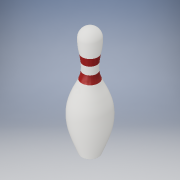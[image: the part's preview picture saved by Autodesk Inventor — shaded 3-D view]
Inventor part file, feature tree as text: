
AUTODESK INVENTOR PART (.ipt)
format: ipt  version: 2017 (Build 210142000, 142)  size: 568,832 bytes
history: native  units: in
note: dims shown in document units (in); Inventor stores cm internally (conversion verified against a paired STEP export)
features: sketch x19, plane x16, other x3, loft x1, revolve x1, fillet x1, extrude x1, chamfer x1
ambient origin geometry x8: Origin, YZ Plane, XZ Plane, XY Plane, X Axis, Y Axis, Z Axis, Center Point
bodies: Body1 (feature_tree)
feature tree (43):
  other  "Bowling Pin"
  sketch  "Sketch1"  dims[d0=2.25in d2=0.75in]
  plane  "Work Plane2"
  sketch  "Sketch2"  dims[d3=2.828in d4=2.25in d5=3.906in]
  plane  "Work Plane3"
  sketch  "Sketch3"  dims[d6=3.375in d7=4.51in]
  plane  "Work Plane4"
  sketch  "Sketch4"  dims[d8=4.5in]
  plane  "Work Plane5"
  sketch  "Sketch5"  dims[d9=4.766in]
  plane  "Work Plane6"
  sketch  "Sketch6"  dims[d10=5.875in]
  plane  "Work Plane7"
  sketch  "Sketch7"  dims[d11=4.563in]
  plane  "Work Plane8"
  sketch  "Sketch8"  dims[d12=7.25in]
  plane  "Work Plane9"
  sketch  "Sketch9"  dims[d13=3.703in]
  plane  "Work Plane10"
  sketch  "Sketch10"  dims[d14=8.625in]
  plane  "Work Plane11"
  sketch  "Sketch11"  dims[d15=2.472in]
  plane  "Work Plane12"
  sketch  "Sketch12"  dims[d16=9.375in]
  plane  "Work Plane13"
  sketch  "Sketch13"  dims[d17=1.965in]
  plane  "Work Plane14"
  sketch  "Sketch14"  dims[d18=10.0in]
  plane  "Work Plane16"
  loft  "Loft3"
  revolve  "Revolution2"  [1 undecoded]
  fillet  "Fillet1"  Radius=3.906in
  extrude  "Extrusion1"  Depth=4.51in
  chamfer  "Chamfer1"  Distance=12.625in
  plane  "Work Plane18"
  other  "Bottom Stripe"
  other  "Top Stripe"
  plane  "Work Plane15"
  sketch  "Sketch17"  dims[d19=1.797in]
  sketch  "Sketch18"  dims[d20=10.875in]
  sketch  "Sketch19"  dims[d21=1.87in]
  sketch  "Sketch21"  dims[d22=11.75in]
  sketch  "Sketch22"  dims[d23=2.094in d24=12.625in d25=2.406in d26=13.5in d27=2.547in d28=15.0in d29=-1.273in d61=1.273in d66=0.0in d67=90.0deg d68=0.0in d69=90.0deg d70=0.0in d71=90.0deg d72=0.0in d73=90.0deg d74=0.0in d75=90.0deg d76=0.0in d77=90.0deg d78=0.0in d79=90.0deg d80=0.0in d81=90.0deg d82=0.0in d83=90.0deg d84=0.0in d85=90.0deg d86=0.0in d87=90.0deg d88=0.0in d89=90.0deg d90=0.0in d91=90.0deg d92=0.0in d93=90.0deg d94=0.0in d95=90.0deg d96=360.0deg d108=0.156in d109=0.4218in d110=2.0in d111=0.0in d112=0.125in d113=0.1641in d114=45.0deg d118=5.125in d119=1.0in d120=4.3808in d121=0.0in d122=0.0in d123=1.0in d124=4.1151in d125=0.0in d126=0.0in]
note: 1 required parameter value undecoded (feature->parameter linkage not recoverable at this tier; creation-order binding heuristic only, values carry confidence <= 0.55)
